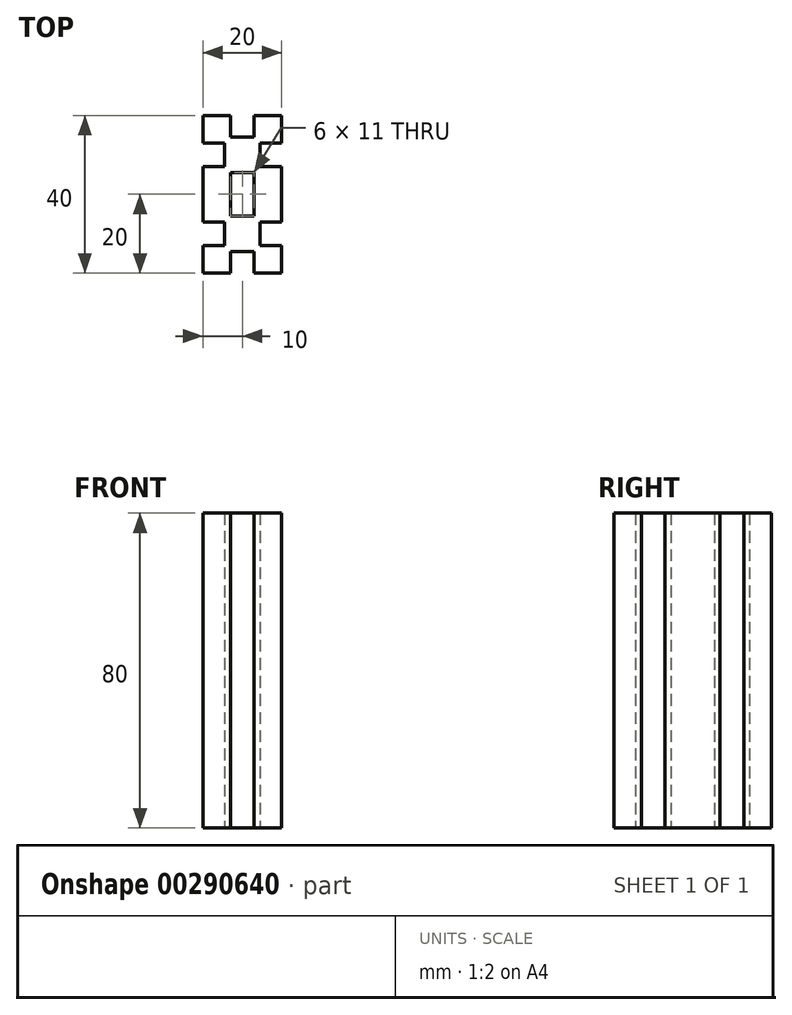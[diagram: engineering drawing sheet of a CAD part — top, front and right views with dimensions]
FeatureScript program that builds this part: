
annotation { "Feature Type Name" : "Feature", "Feature Type Description" : "" }
export const myFeature = defineFeature(function(context is Context, id is Id, definition is map)
    precondition{}
    {
        {
            var Q0;
            Q0=qCreatedBy(makeId("Top.planeOp"),FACE);
            var sketch = newSketch(context, id + "F0", { "sketchPlane" : qUnion([Q0])});
            skLineSegment(sketch, "E0.bottom", {"start": v(0, 0) * mm, "end": v(7, 0) * mm});
            skLineSegment(sketch, "E0.top", {"start": v(0, 20) * mm, "end": v(20, 20) * mm});
            skLineSegment(sketch, "E0.left", {"start": v(0, 0) * mm, "end": v(0, 20) * mm});
            skLineSegment(sketch, "E0.right", {"start": v(20, 0) * mm, "end": v(20, 20) * mm});
            skLineSegment(sketch, "E1.bottom", {"start": v(7, 20) * mm, "end": v(13, 20) * mm});
            skLineSegment(sketch, "E1.top", {"start": v(7, 14.5) * mm, "end": v(13, 14.5) * mm});
            skLineSegment(sketch, "E1.left", {"start": v(7, 20) * mm, "end": v(7, 14.5) * mm});
            skLineSegment(sketch, "E1.right", {"start": v(13, 20) * mm, "end": v(13, 14.5) * mm});
            skLineSegment(sketch, "E2.bottom", {"start": v(20, 13) * mm, "end": v(14.5, 13) * mm});
            skLineSegment(sketch, "E2.top", {"start": v(20, 7) * mm, "end": v(14.5, 7) * mm});
            skLineSegment(sketch, "E2.left", {"start": v(20, 13) * mm, "end": v(20, 7) * mm});
            skLineSegment(sketch, "E2.right", {"start": v(14.5, 13) * mm, "end": v(14.5, 7) * mm});
            skLineSegment(sketch, "E3.top", {"start": v(13, 5.5) * mm, "end": v(7, 5.5) * mm});
            skLineSegment(sketch, "E3.left", {"start": v(13, 0) * mm, "end": v(13, 5.5) * mm});
            skLineSegment(sketch, "E3.right", {"start": v(7, 0) * mm, "end": v(7, 5.5) * mm});
            skLineSegment(sketch, "E4.bottom", {"start": v(0, 7) * mm, "end": v(5.5, 7) * mm});
            skLineSegment(sketch, "E4.top", {"start": v(0, 13) * mm, "end": v(5.5, 13) * mm});
            skLineSegment(sketch, "E4.left", {"start": v(0, 7) * mm, "end": v(0, 13) * mm});
            skLineSegment(sketch, "E4.right", {"start": v(5.5, 7) * mm, "end": v(5.5, 13) * mm});
            skLineSegment(sketch, "E5.MirrorCS", {"start": v(5.5, -7) * mm, "end": v(5.5, -13) * mm});
            skLineSegment(sketch, "E6.MirrorCS", {"start": v(13, -5.5) * mm, "end": v(7, -5.5) * mm});
            skLineSegment(sketch, "E7.MirrorCS", {"start": v(0, -20) * mm, "end": v(20, -20) * mm});
            skLineSegment(sketch, "E8.MirrorCS", {"start": v(7, -20) * mm, "end": v(13, -20) * mm});
            skLineSegment(sketch, "E9.MirrorCS", {"start": v(7, -14.5) * mm, "end": v(13, -14.5) * mm});
            skLineSegment(sketch, "E10.MirrorCS", {"start": v(7, -20) * mm, "end": v(7, -14.5) * mm});
            skLineSegment(sketch, "E11.MirrorCS", {"start": v(13, -20) * mm, "end": v(13, -14.5) * mm});
            skLineSegment(sketch, "E12.MirrorCS", {"start": v(20, -13) * mm, "end": v(14.5, -13) * mm});
            skLineSegment(sketch, "E13.MirrorCS", {"start": v(20, -7) * mm, "end": v(14.5, -7) * mm});
            skLineSegment(sketch, "E14.MirrorCS", {"start": v(20, -13) * mm, "end": v(20, -7) * mm});
            skLineSegment(sketch, "E15.MirrorCS", {"start": v(14.5, -13) * mm, "end": v(14.5, -7) * mm});
            skLineSegment(sketch, "E16.MirrorCS", {"start": v(0, -7) * mm, "end": v(5.5, -7) * mm});
            skLineSegment(sketch, "E17.MirrorCS", {"start": v(0, -13) * mm, "end": v(5.5, -13) * mm});
            skLineSegment(sketch, "E18.MirrorCS", {"start": v(0, -7) * mm, "end": v(0, -13) * mm});
            skLineSegment(sketch, "E19.MirrorCS", {"start": v(7, 0) * mm, "end": v(7, -5.5) * mm});
            skLineSegment(sketch, "E20.MirrorCS", {"start": v(20, 0) * mm, "end": v(20, -20) * mm});
            skLineSegment(sketch, "E21.MirrorCS", {"start": v(0, 0) * mm, "end": v(0, -20) * mm});
            skLineSegment(sketch, "E22.MirrorCS", {"start": v(13, 0) * mm, "end": v(13, -5.5) * mm});
            skLineSegment(sketch, "E23.trimOffspring", {"start": v(13, 0) * mm, "end": v(20, 0) * mm});
            skSolve(sketch);
        }
        {
            var Q0;
            Q0=makeQuery(id+"F0.imprint","IMPRINT",FACE,{"disambiguationData":[TD([[makeQuery(id+"F0.imprint","IMPRINT",EDGE,{"derivedFrom":sQuery(id+"F0.wireOp",EDGE,"E1.top")}),-1.0]])]});
            var Q1;
            {var subQ8=sQuery(id+"F0.wireOp",EDGE,"E0.bottom");Q1=makeQuery(id+"F0.imprint","IMPRINT",FACE,{"disambiguationData":[TD([[makeQuery(id+"F0.imprint","IMPRINT",EDGE,{"derivedFrom":subQ8}),-1.0]])]});}
            extrude(context, id + "F1", {"entities" : qUnion([Q0, Q1]), "depth" : 80 * mm});
        }
    });
